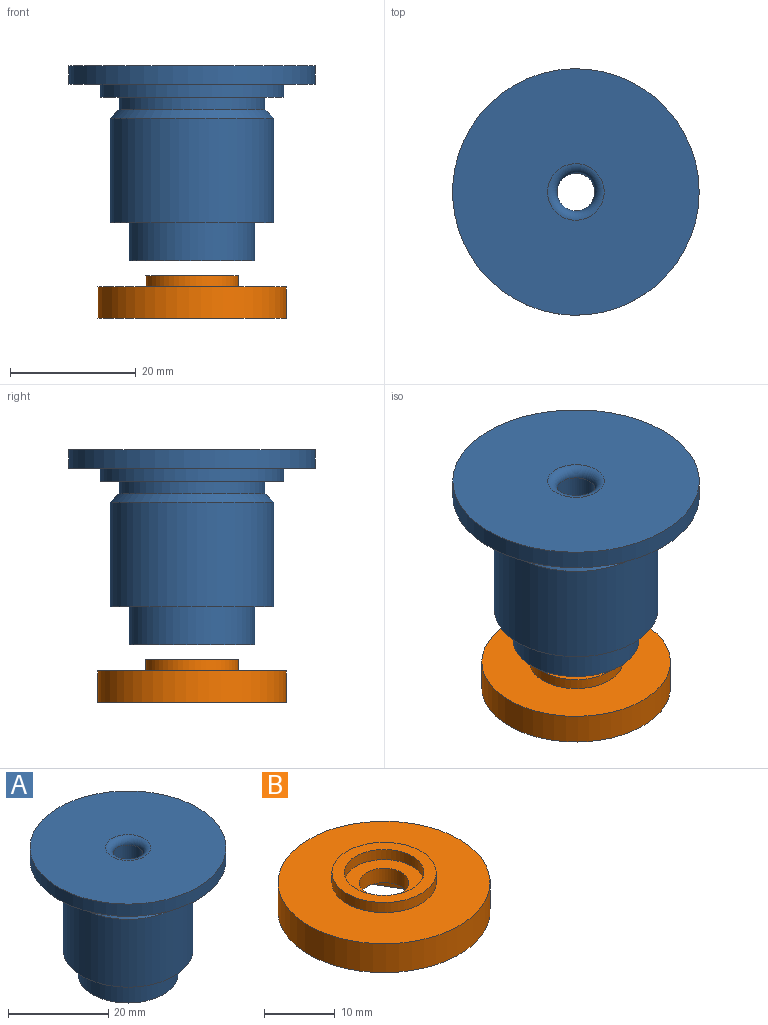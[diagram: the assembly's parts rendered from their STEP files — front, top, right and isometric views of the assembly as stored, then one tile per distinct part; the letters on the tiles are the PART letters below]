
ASSEMBLY  parts=2 mates=1
PART A: 17 faces, bbox 39.2x39.2x31 mm
  f0: cylinder r=7.5mm len=15mm, axis (0,0,1), area 94.2mm2, adj f1,f16
  f1: plane 20x20mm, normal (0,0,-1), area 137.4mm2, adj f0,f2
  f2: cylinder r=10mm len=20mm, axis (0,0,1), area 377mm2, adj f1,f3
  f3: plane 26x26mm, normal (0,0,-1), area 216.8mm2, adj f2,f4
  f4: cylinder r=13mm len=26mm, axis (0,0,1), area 1355.9mm2, adj f3,f5
  f5: cone r=11.6mm half-angle=45deg, axis (0,0,-1), area 153mm2, adj f4,f6
  f6: cylinder r=11.6mm len=23.2mm, axis (0,0,1), area 145.8mm2, adj f5,f7
  f7: plane 29.2x29.2mm, normal (0,0,-1), area 246.9mm2, adj f6,f8
  f8: cylinder r=14.6mm len=29.2mm, axis (0,0,1), area 183.5mm2, adj f7,f9
  f9: plane 39.2x39.2mm, normal (0,0,-1), area 537.2mm2, adj f8,f10
  f10: cylinder r=19.6mm len=39.2mm, axis (0,0,1), area 369.5mm2, adj f9,f11
  f11: plane 39.2x39.2mm, normal (0,0,1), area 1143.3mm2, adj f10,f12
  f12: torus R=4.5mm, axis (0,0,1), area 52.5mm2, adj f11,f13
  f13: cylinder r=3mm len=29.5mm, axis (0,0,1), area 556.1mm2, adj f12,f14
  f14: plane 11x11mm, normal (0,0,-1), area 66.8mm2, adj f13,f15
  f15: cylinder r=5.5mm len=11mm, axis (0,0,1), area 69.1mm2, adj f14,f16
  f16: plane 15x15mm, normal (0,0,-1), area 81.7mm2, adj f0,f15
PART B: 15 faces, bbox 30x30x6.8 mm
  f0: cylinder r=3.5mm len=7mm, axis (0,0,-1), area 55mm2, adj f1,f14
  f1: plane 11.25x11.25mm, normal (0,0,1), area 60.9mm2, adj f0,f5
  f2: cylinder r=15mm len=30mm, axis (0,0,-1), area 471.2mm2, adj f3,f4
  f3: plane 30x30mm, normal (0,0,1), area 536mm2, adj f2,f6
  f4: plane 30x30mm, normal (0,0,-1), area 582.2mm2, adj f2,f8,f9,f10,f11,f12,f13
  f5: cylinder r=5.62mm len=11.25mm, axis (0,0,-1), area 61.9mm2, adj f1,f7
  f6: cylinder r=7.38mm len=14.75mm, axis (0,0,-1), area 81.1mm2, adj f3,f7
  f7: plane 14.75x14.75mm, normal (0,0,1), area 71.5mm2, adj f5,f6
  f8: plane 6x3.46mm, normal (-0.87,0.5,0), area 17.3mm2, adj f4,f9,f13,f14
  f9: plane 6.93x2.5mm, normal (0,1,0), area 17.3mm2, adj f4,f8,f10,f14
  f10: plane 6x3.46mm, normal (0.87,0.5,0), area 17.3mm2, adj f4,f9,f11,f14
  f11: plane 6x3.46mm, normal (0.87,-0.5,0), area 17.3mm2, adj f4,f10,f12,f14
  f12: plane 6.93x2.5mm, normal (0,-1,0), area 17.3mm2, adj f4,f11,f13,f14
  f13: plane 6x3.46mm, normal (-0.87,-0.5,0), area 17.3mm2, adj f4,f8,f12,f14
  f14: plane 13.86x12mm, normal (0,0,-1), area 86.2mm2, adj f0,f8,f9,f10,f11,f12,f13
PLACE A t=(-28.05,16.56,-30.42)mm
PLACE B t=(-28.05,16.56,-57.73)mm
MATE cylindrical A.f0 <-> B.f6  axis (0,0,-1) through (-28.05,16.56,-48.52)mm
